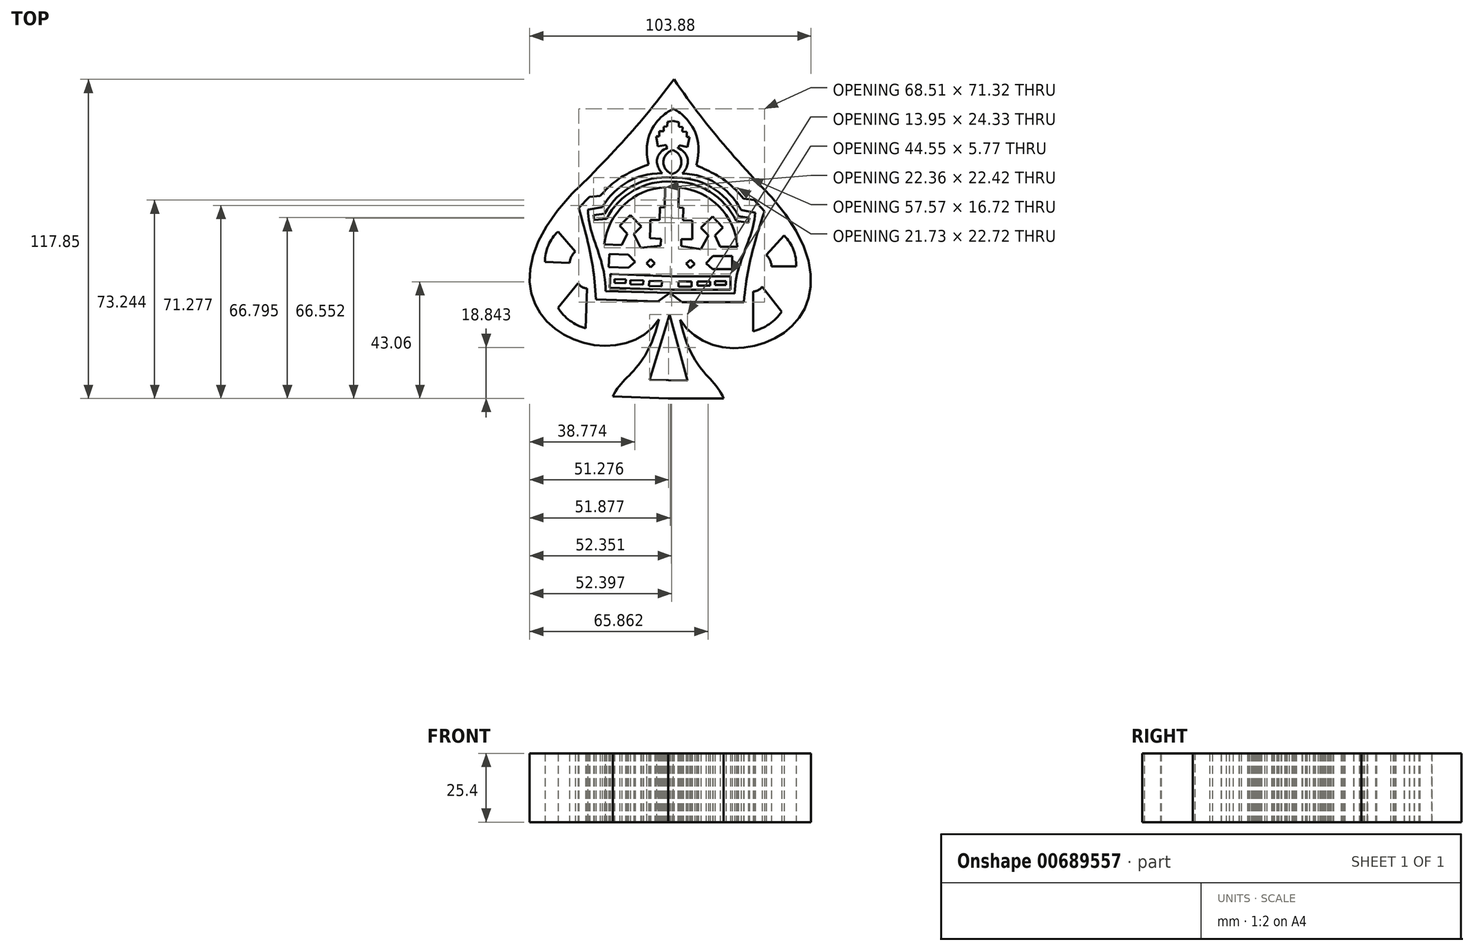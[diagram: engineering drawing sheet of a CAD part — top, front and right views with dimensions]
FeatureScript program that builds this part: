
annotation { "Feature Type Name" : "Feature", "Feature Type Description" : "" }
export const myFeature = defineFeature(function(context is Context, id is Id, definition is map)
    precondition{}
    {
        {
            var Q0;
            Q0=qCreatedBy(makeId("Top.planeOp"),FACE);
            var sketch = newSketch(context, id + "F0", { "sketchPlane" : qUnion([Q0])});
            skFitSpline(sketch, "E0", {"points": [v(-2.53, -37.9) * mm, v(-18.56, -8.8) * mm], "startDerivative": vector(-10, 25.18) * mm, "endDerivative": vector(-11.98, 58.7) * mm});
            skFitSpline(sketch, "E1", {"points": [v(-18.56, -8.8) * mm, v(8.92, 43.01) * mm], "startDerivative": vector(48.1, -79.64) * mm, "endDerivative": vector(-160.88, 156.33) * mm});
            skFitSpline(sketch, "E2", {"points": [v(8.92, 43.01) * mm, v(-20.9, 79.96) * mm], "startDerivative": vector(-37.04, 40.28) * mm, "endDerivative": vector(-28.87, 41.7) * mm});
            skLineSegment(sketch, "E3", {"start": v(-73.33, 8.06) * mm, "end": v(29.07, 0) * mm, "construction": true});
            skLineSegment(sketch, "E4", {"start": v(-2.53, -37.9) * mm, "end": v(-43.46, -37.9) * mm, "construction": true});
            skLineSegment(sketch, "E5", {"start": v(-23, -37.9) * mm, "end": v(-2.53, -37.9) * mm});
            skLineSegment(sketch, "E6", {"start": v(-23, -37.9) * mm, "end": v(-20.9, 79.96) * mm, "construction": true});
            skFitSpline(sketch, "E7.MirrorCS", {"points": [v(-52, 44.1) * mm, v(-20.9, 79.96) * mm], "startDerivative": vector(38.45, 38.94) * mm, "endDerivative": vector(30.34, 40.65) * mm});
            skFitSpline(sketch, "E8.MirrorCS", {"points": [v(-26.39, -8.66) * mm, v(-52, 44.1) * mm], "startDerivative": vector(-50.9, -77.88) * mm, "endDerivative": vector(166.34, 150.5) * mm});
            skFitSpline(sketch, "E9.MirrorCS", {"points": [v(-43.45, -37.16) * mm, v(-26.39, -8.66) * mm], "startDerivative": vector(10.89, 24.8) * mm, "endDerivative": vector(14.06, 58.23) * mm});
            skLineSegment(sketch, "E10.MirrorCS", {"start": v(-23, -37.9) * mm, "end": v(-43.45, -37.16) * mm});
            skFitSpline(sketch, "E11", {"points": [v(-22.32, 0) * mm, v(7.76, 41.99) * mm], "startDerivative": vector(35, -98.07) * mm, "endDerivative": vector(-155.79, 159.42) * mm});
            skLineSegment(sketch, "E12", {"start": v(7.76, 41.99) * mm, "end": v(-20.97, 75.69) * mm});
            skFitSpline(sketch, "E13.MirrorCS", {"points": [v(-22.32, 0) * mm, v(-50.89, 43.03) * mm], "startDerivative": vector(-38.47, -96.76) * mm, "endDerivative": vector(161.36, 153.78) * mm});
            skLineSegment(sketch, "E14.MirrorCS", {"start": v(-50.89, 43.03) * mm, "end": v(-20.97, 75.69) * mm});
            skFitSpline(sketch, "E15", {"points": [v(-21.1, 69) * mm, v(-12.63, 48.2) * mm], "startDerivative": vector(-3.17, 1.85) * mm, "endDerivative": vector(-12.5, -47.35) * mm});
            skFitSpline(sketch, "E16", {"points": [v(-12.63, 48.2) * mm, v(4.86, 35.93) * mm], "startDerivative": vector(24.47, -10.82) * mm, "endDerivative": vector(17.62, -20.68) * mm});
            skLineSegment(sketch, "E17", {"start": v(4.86, 35.93) * mm, "end": v(8.75, 35.43) * mm});
            skLineSegment(sketch, "E18", {"start": v(8.75, 35.43) * mm, "end": v(12.5, 31.25) * mm});
            skFitSpline(sketch, "E19", {"points": [v(12.5, 31.25) * mm, v(4.93, -2.27) * mm], "startDerivative": vector(-13.3, -42.42) * mm, "endDerivative": vector(-3.8, -40.26) * mm});
            skLineSegment(sketch, "E20", {"start": v(4.93, -2.27) * mm, "end": v(-17.9, -2.27) * mm});
            skLineSegment(sketch, "E21", {"start": v(-17.9, -2.27) * mm, "end": v(-22.3, 1.14) * mm});
            skLineSegment(sketch, "E22", {"start": v(-22.3, 1.14) * mm, "end": v(1.58, 0.9) * mm});
            skFitSpline(sketch, "E23", {"points": [v(1.58, 0.9) * mm, v(9.1, 30.71) * mm], "startDerivative": vector(0.02, 34.28) * mm, "endDerivative": vector(0.64, 27.66) * mm});
            skLineSegment(sketch, "E24", {"start": v(9.1, 30.71) * mm, "end": v(3.9, 31.77) * mm});
            skFitSpline(sketch, "E25", {"points": [v(3.9, 31.77) * mm, v(-17.82, 45.13) * mm], "startDerivative": vector(-2.54, 4.45) * mm, "endDerivative": vector(-44.2, 0.64) * mm});
            skFitSpline(sketch, "E26", {"points": [v(-17.82, 45.13) * mm, v(-19.45, 54.64) * mm], "startDerivative": vector(6.8, 6.6) * mm, "endDerivative": vector(-16.6, 7.97) * mm});
            skFitSpline(sketch, "E27", {"points": [v(-19.45, 54.64) * mm, v(-18.91, 55.61) * mm], "startDerivative": vector(1.1, 0.75) * mm, "endDerivative": vector(0.26, 1.43) * mm});
            skLineSegment(sketch, "E28", {"start": v(-18.91, 55.61) * mm, "end": v(-15.88, 55.02) * mm});
            skLineSegment(sketch, "E29", {"start": v(-15.88, 55.02) * mm, "end": v(-15.16, 58.67) * mm});
            skLineSegment(sketch, "E30", {"start": v(-15.16, 58.67) * mm, "end": v(-16.2, 58.69) * mm});
            skLineSegment(sketch, "E31", {"start": v(-16.2, 58.69) * mm, "end": v(-16.2, 60.6) * mm});
            skLineSegment(sketch, "E32", {"start": v(-16.2, 60.6) * mm, "end": v(-17.81, 60.63) * mm});
            skLineSegment(sketch, "E33", {"start": v(-17.81, 60.63) * mm, "end": v(-17.71, 62.36) * mm});
            skLineSegment(sketch, "E34", {"start": v(-17.71, 62.36) * mm, "end": v(-19.06, 62.48) * mm});
            skLineSegment(sketch, "E35", {"start": v(-19.06, 62.48) * mm, "end": v(-19.06, 64.14) * mm});
            skLineSegment(sketch, "E36", {"start": v(-19.06, 64.14) * mm, "end": v(-21.17, 64.57) * mm});
            skLineSegment(sketch, "E37.MirrorCS", {"start": v(-23.3, 64.21) * mm, "end": v(-21.17, 64.57) * mm});
            skLineSegment(sketch, "E38.MirrorCS", {"start": v(-23.35, 62.55) * mm, "end": v(-23.3, 64.21) * mm});
            skLineSegment(sketch, "E39.MirrorCS", {"start": v(-24.7, 62.49) * mm, "end": v(-23.35, 62.55) * mm});
            skLineSegment(sketch, "E40.MirrorCS", {"start": v(-24.67, 60.75) * mm, "end": v(-24.7, 62.49) * mm});
            skLineSegment(sketch, "E41.MirrorCS", {"start": v(-26.29, 60.78) * mm, "end": v(-24.67, 60.75) * mm});
            skLineSegment(sketch, "E42.MirrorCS", {"start": v(-26.36, 58.87) * mm, "end": v(-26.29, 60.78) * mm});
            skLineSegment(sketch, "E43.MirrorCS", {"start": v(-27.38, 58.89) * mm, "end": v(-26.36, 58.87) * mm});
            skLineSegment(sketch, "E44.MirrorCS", {"start": v(-26.8, 55.21) * mm, "end": v(-27.38, 58.89) * mm});
            skLineSegment(sketch, "E45.MirrorCS", {"start": v(-23.75, 55.7) * mm, "end": v(-26.8, 55.21) * mm});
            skFitSpline(sketch, "E46.MirrorCS", {"points": [v(-23.24, 54.71) * mm, v(-23.75, 55.7) * mm], "startDerivative": vector(-1.07, 0.79) * mm, "endDerivative": vector(-0.2, 1.44) * mm});
            skFitSpline(sketch, "E47.MirrorCS", {"points": [v(-25.2, 45.26) * mm, v(-23.24, 54.71) * mm], "startDerivative": vector(-6.57, 6.83) * mm, "endDerivative": vector(16.88, 7.38) * mm});
            skFitSpline(sketch, "E48.MirrorCS", {"points": [v(-47.4, 32.69) * mm, v(-25.2, 45.26) * mm], "startDerivative": vector(2.7, 4.36) * mm, "endDerivative": vector(44.19, -0.94) * mm});
            skLineSegment(sketch, "E49.MirrorCS", {"start": v(-52.62, 31.81) * mm, "end": v(-47.4, 32.69) * mm});
            skFitSpline(sketch, "E50.MirrorCS", {"points": [v(-46.17, 1.74) * mm, v(-52.62, 31.81) * mm], "startDerivative": vector(1.2, 34.26) * mm, "endDerivative": vector(0.35, 27.66) * mm});
            skLineSegment(sketch, "E51.MirrorCS", {"start": v(-22.3, 1.14) * mm, "end": v(-46.17, 1.74) * mm});
            skLineSegment(sketch, "E52.MirrorCS", {"start": v(-26.81, -2.11) * mm, "end": v(-22.3, 1.14) * mm});
            skLineSegment(sketch, "E53.MirrorCS", {"start": v(-49.63, -1.3) * mm, "end": v(-26.81, -2.11) * mm});
            skFitSpline(sketch, "E54.MirrorCS", {"points": [v(-56.01, 32.47) * mm, v(-49.63, -1.3) * mm], "startDerivative": vector(11.78, -42.87) * mm, "endDerivative": vector(2.37, -40.37) * mm});
            skLineSegment(sketch, "E55.MirrorCS", {"start": v(-52.1, 36.52) * mm, "end": v(-56.01, 32.47) * mm});
            skLineSegment(sketch, "E56.MirrorCS", {"start": v(-48.2, 36.87) * mm, "end": v(-52.1, 36.52) * mm});
            skFitSpline(sketch, "E57.MirrorCS", {"points": [v(-30.29, 48.51) * mm, v(-48.2, 36.87) * mm], "startDerivative": vector(-24.84, -9.94) * mm, "endDerivative": vector(-18.34, -20.04) * mm});
            skFitSpline(sketch, "E58.MirrorCS", {"points": [v(-21.1, 69) * mm, v(-30.29, 48.51) * mm], "startDerivative": vector(3.23, 1.74) * mm, "endDerivative": vector(10.81, -47.77) * mm});
            skArc(sketch, "E59", {"start": v(-21.52, 45) * mm, "mid": v(-18.12, 49.33) * mm, "end": v(-21.36, 53.79) * mm});
            skArc(sketch, "E60", {"start": v(2.89, 29.49) * mm, "mid": v(-7.22, 40.2) * mm, "end": v(-21.54, 43.65) * mm});
            skLineSegment(sketch, "E61", {"start": v(2.89, 29.49) * mm, "end": v(6.98, 28.8) * mm});
            skLineSegment(sketch, "E62", {"start": v(6.98, 28.8) * mm, "end": v(6.61, 27) * mm});
            skLineSegment(sketch, "E63", {"start": v(6.61, 27) * mm, "end": v(2.1, 27.63) * mm});
            skArc(sketch, "E64", {"start": v(2.1, 27.63) * mm, "mid": v(-7.57, 38.43) * mm, "end": v(-21.57, 42.2) * mm});
            skLineSegment(sketch, "E65", {"start": v(-19.02, 40.02) * mm, "end": v(-19.15, 32.56) * mm});
            skLineSegment(sketch, "E66", {"start": v(-19.15, 32.56) * mm, "end": v(-17.43, 32.53) * mm});
            skLineSegment(sketch, "E67", {"start": v(-17.43, 32.53) * mm, "end": v(-17.51, 27.87) * mm});
            skLineSegment(sketch, "E68", {"start": v(-17.51, 27.87) * mm, "end": v(-14.09, 27.8) * mm});
            skLineSegment(sketch, "E69", {"start": v(-14.09, 27.8) * mm, "end": v(-14.14, 25.18) * mm});
            skLineSegment(sketch, "E70", {"start": v(-14.14, 25.18) * mm, "end": v(-14.14, 20.98) * mm});
            skLineSegment(sketch, "E71", {"start": v(-14.14, 20.98) * mm, "end": v(-18.2, 20.98) * mm});
            skLineSegment(sketch, "E72", {"start": v(-18.2, 20.98) * mm, "end": v(-18.2, 18.43) * mm});
            skLineSegment(sketch, "E73", {"start": v(-18.2, 18.43) * mm, "end": v(-10.92, 17.3) * mm});
            skLineSegment(sketch, "E74", {"start": v(-10.92, 17.3) * mm, "end": v(-8.1, 22.3) * mm});
            skLineSegment(sketch, "E75", {"start": v(-8.1, 22.3) * mm, "end": v(-10.89, 25.18) * mm});
            skLineSegment(sketch, "E76", {"start": v(-10.89, 25.18) * mm, "end": v(-6.67, 29.26) * mm});
            skLineSegment(sketch, "E77", {"start": v(-6.67, 29.26) * mm, "end": v(-2.8, 25.25) * mm});
            skLineSegment(sketch, "E78", {"start": v(-2.8, 25.25) * mm, "end": v(-5.78, 22.36) * mm});
            skLineSegment(sketch, "E79", {"start": v(-5.78, 22.36) * mm, "end": v(-3.84, 18.15) * mm});
            skLineSegment(sketch, "E80", {"start": v(-3.84, 18.15) * mm, "end": v(2.58, 18.15) * mm});
            skArc(sketch, "E81", {"start": v(2.58, 18.15) * mm, "mid": v(-4.22, 33.04) * mm, "end": v(-19.02, 40.02) * mm});
            skArc(sketch, "E82.MirrorCS", {"start": v(-46.46, 30.37) * mm, "mid": v(-35.98, 40.72) * mm, "end": v(-21.54, 43.65) * mm});
            skLineSegment(sketch, "E83.MirrorCS", {"start": v(-46.46, 30.37) * mm, "end": v(-50.58, 29.82) * mm});
            skArc(sketch, "E84.MirrorCS", {"start": v(-21.52, 45) * mm, "mid": v(-24.76, 49.45) * mm, "end": v(-21.36, 53.79) * mm});
            skLineSegment(sketch, "E85.MirrorCS", {"start": v(-50.58, 29.82) * mm, "end": v(-50.28, 28) * mm});
            skLineSegment(sketch, "E86.MirrorCS", {"start": v(-50.28, 28) * mm, "end": v(-45.75, 28.48) * mm});
            skArc(sketch, "E87.MirrorCS", {"start": v(-45.75, 28.48) * mm, "mid": v(-35.7, 38.93) * mm, "end": v(-21.57, 42.2) * mm});
            skArc(sketch, "E88.MirrorCS", {"start": v(-46.56, 19.03) * mm, "mid": v(-39.24, 33.67) * mm, "end": v(-24.2, 40.12) * mm});
            skLineSegment(sketch, "E89.MirrorCS", {"start": v(-24.2, 40.12) * mm, "end": v(-24.33, 32.65) * mm});
            skLineSegment(sketch, "E90.MirrorCS", {"start": v(-24.33, 32.65) * mm, "end": v(-26.05, 32.68) * mm});
            skLineSegment(sketch, "E91.MirrorCS", {"start": v(-26.05, 32.68) * mm, "end": v(-26.13, 28.02) * mm});
            skLineSegment(sketch, "E92.MirrorCS", {"start": v(-26.13, 28.02) * mm, "end": v(-29.56, 28.08) * mm});
            skLineSegment(sketch, "E93.MirrorCS", {"start": v(-29.56, 28.08) * mm, "end": v(-29.6, 25.45) * mm});
            skLineSegment(sketch, "E94.MirrorCS", {"start": v(-29.6, 25.45) * mm, "end": v(-29.75, 21.26) * mm});
            skLineSegment(sketch, "E95.MirrorCS", {"start": v(-29.75, 21.26) * mm, "end": v(-25.7, 21.12) * mm});
            skLineSegment(sketch, "E96.MirrorCS", {"start": v(-25.7, 21.12) * mm, "end": v(-25.8, 18.57) * mm});
            skLineSegment(sketch, "E97.MirrorCS", {"start": v(-25.8, 18.57) * mm, "end": v(-33.1, 17.7) * mm});
            skLineSegment(sketch, "E98.MirrorCS", {"start": v(-33.1, 17.7) * mm, "end": v(-35.74, 22.8) * mm});
            skLineSegment(sketch, "E99.MirrorCS", {"start": v(-35.74, 22.8) * mm, "end": v(-32.85, 25.57) * mm});
            skLineSegment(sketch, "E100.MirrorCS", {"start": v(-32.85, 25.57) * mm, "end": v(-36.92, 29.8) * mm});
            skLineSegment(sketch, "E101.MirrorCS", {"start": v(-36.92, 29.8) * mm, "end": v(-40.93, 25.93) * mm});
            skLineSegment(sketch, "E102.MirrorCS", {"start": v(-40.93, 25.93) * mm, "end": v(-38.05, 22.93) * mm});
            skLineSegment(sketch, "E103.MirrorCS", {"start": v(-38.05, 22.93) * mm, "end": v(-40.14, 18.8) * mm});
            skLineSegment(sketch, "E104.MirrorCS", {"start": v(-40.14, 18.8) * mm, "end": v(-46.56, 19.03) * mm});
            skLineSegment(sketch, "E105.bottom", {"start": v(-22.06, 14.7) * mm, "end": v(0.65, 14.7) * mm});
            skLineSegment(sketch, "E105.top", {"start": v(-22.06, 9.84) * mm, "end": v(0.65, 9.84) * mm});
            skLineSegment(sketch, "E105.right", {"start": v(0.65, 14.7) * mm, "end": v(0.65, 9.84) * mm});
            skLineSegment(sketch, "E106.bottom", {"start": v(-22.2, 7.26) * mm, "end": v(0, 7.26) * mm});
            skLineSegment(sketch, "E106.top", {"start": v(-22.28, 2.29) * mm, "end": v(0, 2.29) * mm});
            skLineSegment(sketch, "E106.right", {"start": v(0, 7.26) * mm, "end": v(0, 2.29) * mm});
            skLineSegment(sketch, "E107.MirrorCS", {"start": v(-22.06, 14.7) * mm, "end": v(-44.76, 15.5) * mm});
            skLineSegment(sketch, "E108.MirrorCS", {"start": v(-22.23, 9.85) * mm, "end": v(-44.93, 10.66) * mm});
            skLineSegment(sketch, "E109.MirrorCS", {"start": v(-22.2, 7.26) * mm, "end": v(-44.37, 8.05) * mm});
            skLineSegment(sketch, "E110.MirrorCS", {"start": v(-22.28, 2.29) * mm, "end": v(-44.55, 3.08) * mm});
            skLineSegment(sketch, "E111.MirrorCS", {"start": v(-44.37, 8.05) * mm, "end": v(-44.55, 3.08) * mm});
            skLineSegment(sketch, "E112.MirrorCS", {"start": v(-44.76, 15.5) * mm, "end": v(-44.93, 10.66) * mm});
            skLineSegment(sketch, "E113.bottom", {"start": v(-5.78, 5.45) * mm, "end": v(-1.65, 5.45) * mm});
            skLineSegment(sketch, "E113.top", {"start": v(-5.78, 4.02) * mm, "end": v(-1.65, 4.02) * mm});
            skLineSegment(sketch, "E113.left", {"start": v(-5.78, 5.45) * mm, "end": v(-5.78, 4.02) * mm});
            skLineSegment(sketch, "E113.right", {"start": v(-1.65, 5.45) * mm, "end": v(-1.65, 4.02) * mm});
            skLineSegment(sketch, "E114.bottom", {"start": v(-12.25, 5.3) * mm, "end": v(-7.48, 5.3) * mm});
            skLineSegment(sketch, "E114.top", {"start": v(-12.25, 3.82) * mm, "end": v(-7.48, 3.82) * mm});
            skLineSegment(sketch, "E114.left", {"start": v(-12.25, 5.3) * mm, "end": v(-12.25, 3.82) * mm});
            skLineSegment(sketch, "E114.right", {"start": v(-7.48, 5.3) * mm, "end": v(-7.48, 3.82) * mm});
            skLineSegment(sketch, "E115.bottom", {"start": v(-19.15, 5.33) * mm, "end": v(-14.41, 5.33) * mm});
            skLineSegment(sketch, "E115.top", {"start": v(-19.15, 3.42) * mm, "end": v(-14.41, 3.42) * mm});
            skLineSegment(sketch, "E115.left", {"start": v(-19.15, 5.33) * mm, "end": v(-19.15, 3.42) * mm});
            skLineSegment(sketch, "E115.right", {"start": v(-14.41, 5.33) * mm, "end": v(-14.41, 3.42) * mm});
            skLineSegment(sketch, "E116.MirrorCS", {"start": v(-25.3, 5.44) * mm, "end": v(-30.04, 5.61) * mm});
            skLineSegment(sketch, "E117.MirrorCS", {"start": v(-25.3, 5.44) * mm, "end": v(-25.36, 3.53) * mm});
            skLineSegment(sketch, "E118.MirrorCS", {"start": v(-25.36, 3.53) * mm, "end": v(-30.1, 3.7) * mm});
            skLineSegment(sketch, "E119.MirrorCS", {"start": v(-30.04, 5.61) * mm, "end": v(-30.1, 3.7) * mm});
            skLineSegment(sketch, "E120.MirrorCS", {"start": v(-32.2, 5.65) * mm, "end": v(-32.25, 4.18) * mm});
            skLineSegment(sketch, "E121.MirrorCS", {"start": v(-32.2, 5.65) * mm, "end": v(-36.96, 5.82) * mm});
            skLineSegment(sketch, "E122.MirrorCS", {"start": v(-36.96, 5.82) * mm, "end": v(-37.01, 4.35) * mm});
            skLineSegment(sketch, "E123.MirrorCS", {"start": v(-32.25, 4.18) * mm, "end": v(-37.01, 4.35) * mm});
            skLineSegment(sketch, "E124.MirrorCS", {"start": v(-38.66, 6.04) * mm, "end": v(-38.71, 4.6) * mm});
            skLineSegment(sketch, "E125.MirrorCS", {"start": v(-38.66, 6.04) * mm, "end": v(-42.79, 6.18) * mm});
            skLineSegment(sketch, "E126.MirrorCS", {"start": v(-42.79, 6.18) * mm, "end": v(-42.84, 4.76) * mm});
            skLineSegment(sketch, "E127.MirrorCS", {"start": v(-38.71, 4.6) * mm, "end": v(-42.84, 4.76) * mm});
            skLineSegment(sketch, "E128", {"start": v(-37.68, 15.25) * mm, "end": v(-40.35, 12.52) * mm});
            skLineSegment(sketch, "E129", {"start": v(-40.35, 12.52) * mm, "end": v(-37.68, 10.4) * mm});
            skLineSegment(sketch, "E130", {"start": v(-37.68, 10.4) * mm, "end": v(-35.15, 12.52) * mm});
            skLineSegment(sketch, "E131", {"start": v(-35.15, 12.52) * mm, "end": v(-37.68, 15.25) * mm});
            skLineSegment(sketch, "E132", {"start": v(-29.44, 13.52) * mm, "end": v(-30.94, 12.05) * mm});
            skPoint(sketch, "E132.startSnap0", {"position": v(-29.44, 18.13) * mm});
            skLineSegment(sketch, "E133", {"start": v(-30.94, 12.05) * mm, "end": v(-29.44, 10.53) * mm});
            skLineSegment(sketch, "E134", {"start": v(-29.44, 10.53) * mm, "end": v(-27.89, 12.05) * mm});
            skLineSegment(sketch, "E135", {"start": v(-27.89, 12.05) * mm, "end": v(-29.44, 13.52) * mm});
            skLineSegment(sketch, "E136.MirrorCS", {"start": v(-16.33, 11.85) * mm, "end": v(-14.72, 13.26) * mm});
            skLineSegment(sketch, "E137.MirrorCS", {"start": v(-14.72, 13.26) * mm, "end": v(-13.28, 11.74) * mm});
            skLineSegment(sketch, "E138.MirrorCS", {"start": v(-13.28, 11.74) * mm, "end": v(-14.83, 10.27) * mm});
            skLineSegment(sketch, "E139.MirrorCS", {"start": v(-14.83, 10.27) * mm, "end": v(-16.33, 11.85) * mm});
            skLineSegment(sketch, "E140.MirrorCS", {"start": v(-9.06, 12.06) * mm, "end": v(-6.43, 14.7) * mm});
            skLineSegment(sketch, "E141.MirrorCS", {"start": v(-6.43, 14.7) * mm, "end": v(-3.85, 11.87) * mm});
            skLineSegment(sketch, "E142.MirrorCS", {"start": v(-3.85, 11.87) * mm, "end": v(-6.6, 9.84) * mm});
            skLineSegment(sketch, "E143.MirrorCS", {"start": v(-6.6, 9.84) * mm, "end": v(-9.06, 12.06) * mm});
            skArc(sketch, "E144", {"start": v(24.28, 10.85) * mm, "mid": v(23.24, 17.03) * mm, "end": v(19.83, 22.3) * mm});
            skLineSegment(sketch, "E145", {"start": v(24.28, 10.85) * mm, "end": v(15.16, 10.85) * mm});
            skLineSegment(sketch, "E146", {"start": v(19.83, 22.3) * mm, "end": v(13.26, 15.09) * mm});
            skArc(sketch, "E147", {"start": v(15.16, 10.85) * mm, "mid": v(14.6, 13.14) * mm, "end": v(13.26, 15.09) * mm});
            skArc(sketch, "E148", {"start": v(8.35, -13.08) * mm, "mid": v(14.29, -10.45) * mm, "end": v(18.87, -5.85) * mm});
            skLineSegment(sketch, "E149", {"start": v(8.35, -13.08) * mm, "end": v(8.35, 1.63) * mm});
            skLineSegment(sketch, "E150", {"start": v(18.87, -5.85) * mm, "end": v(11.72, 3.42) * mm});
            skPoint(sketch, "E150.endSnap0", {"position": v(-16.78, 3.42) * mm});
            skArc(sketch, "E151", {"start": v(8.35, 1.63) * mm, "mid": v(10.25, 2.12) * mm, "end": v(11.72, 3.42) * mm});
            skLineSegment(sketch, "E152.MirrorCS", {"start": v(-63.7, -4.38) * mm, "end": v(-56.22, 4.63) * mm});
            skArc(sketch, "E153.MirrorCS", {"start": v(-53.44, -11.98) * mm, "mid": v(-59.28, -9.14) * mm, "end": v(-63.7, -4.38) * mm});
            skArc(sketch, "E154.MirrorCS", {"start": v(-52.92, 2.72) * mm, "mid": v(-54.8, 3.28) * mm, "end": v(-56.22, 4.63) * mm});
            skLineSegment(sketch, "E155.MirrorCS", {"start": v(-53.44, -11.98) * mm, "end": v(-52.92, 2.72) * mm});
            skLineSegment(sketch, "E156.MirrorCS", {"start": v(-68.5, 12.5) * mm, "end": v(-59.4, 12.18) * mm});
            skArc(sketch, "E157.MirrorCS", {"start": v(-59.4, 12.18) * mm, "mid": v(-58.75, 14.45) * mm, "end": v(-57.34, 16.34) * mm});
            skLineSegment(sketch, "E158.MirrorCS", {"start": v(-63.65, 23.78) * mm, "end": v(-57.34, 16.34) * mm});
            skArc(sketch, "E159.MirrorCS", {"start": v(-68.5, 12.5) * mm, "mid": v(-67.25, 18.64) * mm, "end": v(-63.65, 23.78) * mm});
            skLineSegment(sketch, "E160", {"start": v(-23.48, -32.5) * mm, "end": v(-22.9, -32.5) * mm});
            skLineSegment(sketch, "E161.MirrorCS", {"start": v(-22.32, -32.51) * mm, "end": v(-22.9, -32.5) * mm});
            skLineSegment(sketch, "E162", {"start": v(-22.44, -6.88) * mm, "end": v(-15.9, -31.2) * mm});
            skLineSegment(sketch, "E163", {"start": v(-15.9, -31.2) * mm, "end": v(-22.87, -31.09) * mm});
            skLineSegment(sketch, "E164.MirrorCS", {"start": v(-22.44, -6.88) * mm, "end": v(-29.85, -30.96) * mm});
            skLineSegment(sketch, "E165.MirrorCS", {"start": v(-29.85, -30.96) * mm, "end": v(-22.87, -31.09) * mm});
            skSolve(sketch);
        }
        {
            var Q0;
            Q0=makeQuery(id+"F0.imprint","IMPRINT",FACE,{"disambiguationData":[TD([[makeQuery(id+"F0.imprint","IMPRINT",EDGE,{"derivedFrom":sQuery(id+"F0.wireOp",EDGE,"TR8coMyy-DoK1-fhJf-mkVZ-P4jdJu8iWF87")}),-1.0]])]});
            var Q1;
            Q1=makeQuery(id+"F0.imprint","IMPRINT",FACE,{"disambiguationData":[TD([[makeQuery(id+"F0.imprint","IMPRINT",EDGE,{"derivedFrom":sQuery(id+"F0.wireOp",EDGE,"E11")}),1.0]])]});
            var Q2;
            Q2=makeQuery(id+"F0.imprint","IMPRINT",FACE,{"disambiguationData":[TD([[makeQuery(id+"F0.imprint","IMPRINT",EDGE,{"derivedFrom":sQuery(id+"F0.wireOp",EDGE,"E22")}),1.0]])]});
            var Q3;
            Q3=makeQuery(id+"F0.imprint","IMPRINT",FACE,{"disambiguationData":[TD([[makeQuery(id+"F0.imprint","IMPRINT",EDGE,{"derivedFrom":sQuery(id+"F0.wireOp",EDGE,"E113.bottom")}),-1.0]])]});
            var Q4;
            Q4=makeQuery(id+"F0.imprint","IMPRINT",FACE,{"disambiguationData":[TD([[makeQuery(id+"F0.imprint","IMPRINT",EDGE,{"derivedFrom":sQuery(id+"F0.wireOp",EDGE,"E114.bottom")}),-1.0]])]});
            var Q5;
            Q5=makeQuery(id+"F0.imprint","IMPRINT",FACE,{"disambiguationData":[TD([[makeQuery(id+"F0.imprint","IMPRINT",EDGE,{"derivedFrom":sQuery(id+"F0.wireOp",EDGE,"E115.bottom")}),-1.0]])]});
            var Q6;
            Q6=makeQuery(id+"F0.imprint","IMPRINT",FACE,{"disambiguationData":[TD([[makeQuery(id+"F0.imprint","IMPRINT",EDGE,{"derivedFrom":sQuery(id+"F0.wireOp",EDGE,"E116.MirrorCS")}),1.0]])]});
            var Q7;
            Q7=makeQuery(id+"F0.imprint","IMPRINT",FACE,{"disambiguationData":[TD([[makeQuery(id+"F0.imprint","IMPRINT",EDGE,{"derivedFrom":sQuery(id+"F0.wireOp",EDGE,"E120.MirrorCS")}),-1.0]])]});
            var Q8;
            Q8=makeQuery(id+"F0.imprint","IMPRINT",FACE,{"disambiguationData":[TD([[makeQuery(id+"F0.imprint","IMPRINT",EDGE,{"derivedFrom":sQuery(id+"F0.wireOp",EDGE,"E124.MirrorCS")}),-1.0]])]});
            var Q9;
            Q9=makeQuery(id+"F0.imprint","IMPRINT",FACE,{"disambiguationData":[TD([[makeQuery(id+"F0.imprint","IMPRINT",EDGE,{"derivedFrom":sQuery(id+"F0.wireOp",EDGE,"E0")}),1.0]])]});
            extrude(context, id + "F1", {"entities" : qUnion([Q0, Q1, Q2, Q3, Q4, Q5, Q6, Q7, Q8, Q9]), "depth" : 25.4 * mm, "offsetDistance" : 25.4 * mm});
        }
    });
